# Revit family: Storage-Teknion-EMCW_Work_Cabinet-R2016
name_source: partatom
category: Furniture
revit_build: Autodesk Revit 2018 (Build: 20190510_1515(x64)
units: mm (PartAtom-declared; Revit-internal decimal feet)

## family parameters
Always vertical = Yes
Cut with Voids When Loaded = No
OmniClass Number = 23.40.20.00
OmniClass Title = General Furniture and Specialties
Room Calculation Point = No
Shared = Yes
Work Plane-Based = No

## types (5) — shared parameters
Assembly Code = E2020200
Manufacturer = Teknion
Manufacturer Fax = 416.661.4586
Part Number = EMCW
Product Documentation Link = https://assets.teknion.com
Product Line = Emote
Product Page URL = https://www.teknion.com
Series = Emote
Sustainability Data = https://www.teknion.com
URL = www.teknion.com
Unit Weight URL = http://www.teknion.com
Warranty = http://www.teknion.com

## per-type parameters (varying)
| type | Bottom Cabinet Height | Bottom Cabinet Horizontal Pull Visibility | Bottom Cabinet Visibility | Description | Model | Open | Second Shelf Visibility |
| Partial Height Drawer | 13 " | Yes | Yes | Emote Work Cabinet, Partial Height Drawer, 29" Width, 45" Height | EMCWPD2945 | No | Yes |
| Open | 13 " | No | No | Emote Work Cabinet, Open, 29" Width, 45" Height | EMCWOP2945 | Yes | Yes |
| Full Height Drawer | 17.25 " | Yes | Yes | Emote Work Cabinet, Full Height Drawer, 29" Width, 45" Height | EMCWFD2945 | No | No |
| Lower Closed | 17.25 " | No | Yes | Emote Work Cabinet, Lower Closed, 29" Width, 45" Height | EMCWLC2945 | No | No |
| Double Drawers | 13 " | Yes | Yes | Emote Work Cabinet, Double Drawers, 29" Width, 45" Height | EMCWDD2945 | No | Yes |

type visibility flags (boolean, named after types; folded from table):
- Partial Height Drawer: Yes: Partial Height Drawer
- Open: Yes: (none)
- Full Height Drawer: Yes: Full Height Drawer
- Lower Closed: Yes: Lower Closed
- Double Drawers: Yes: Double Drawers

## geometry (parser evidence)
native form markers: Blend x47, Sweep x2
no freeform markers — native parametric forms only
